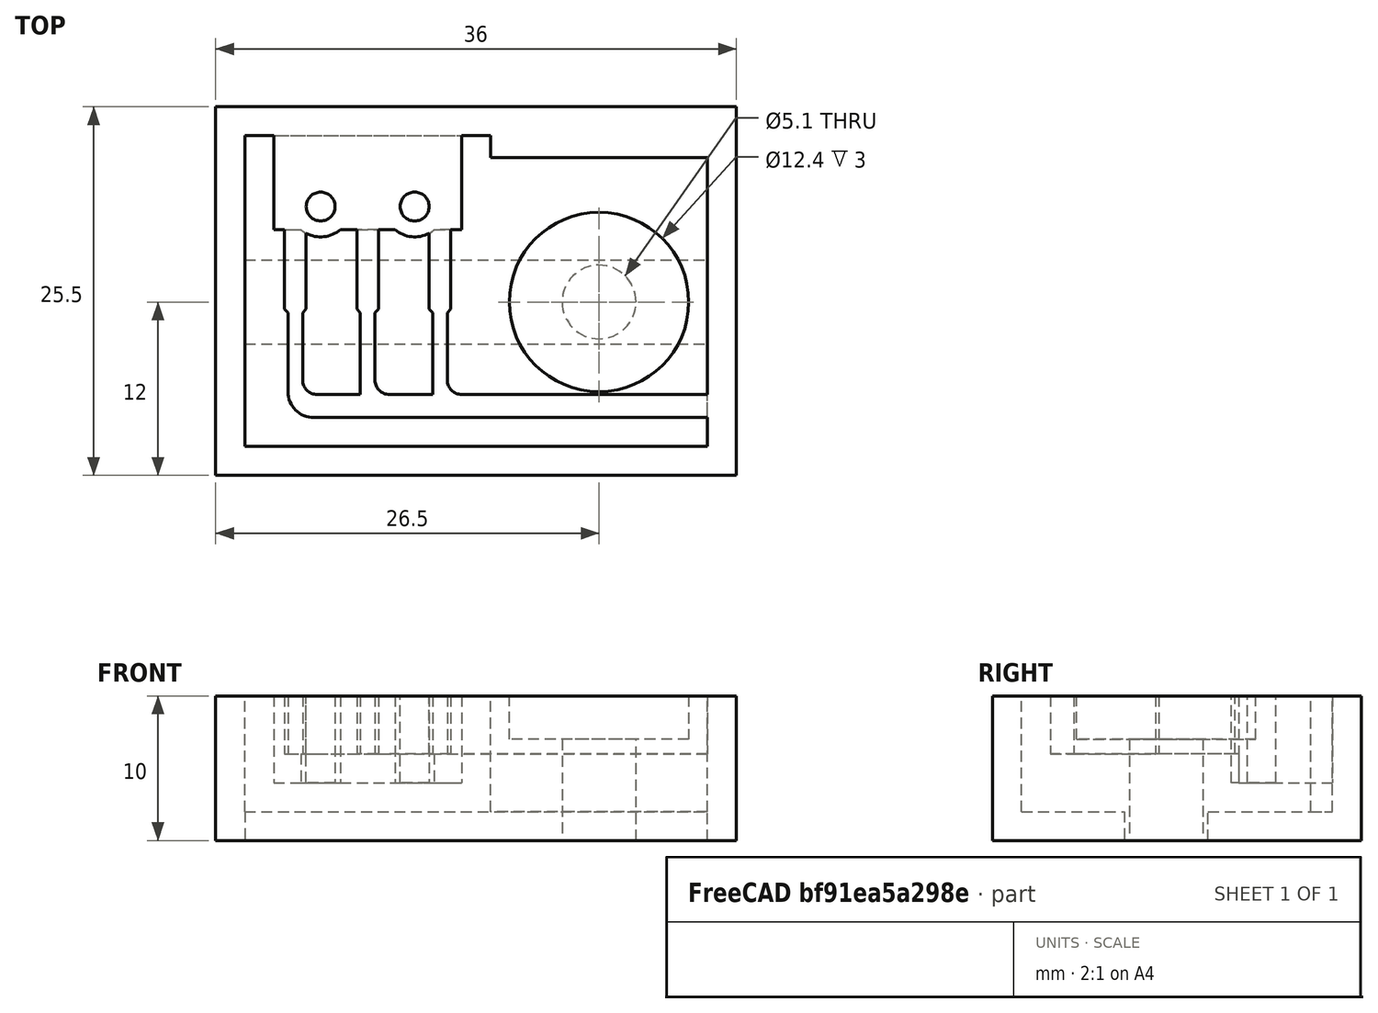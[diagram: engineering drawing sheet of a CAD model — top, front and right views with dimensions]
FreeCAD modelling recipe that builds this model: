
FCSTD DOCUMENT  (FreeCAD 0.18R16131 (Git))
Label: Limit Switch Bed - BottomMirror Job
License: All rights reserved
LicenseURL: http://es.wikipedia.org/wiki/Todos_los_derechos_reservados
objects: Path::FeaturePython×8, Part::Feature×2, Part::FeaturePython×2, Mesh::FeaturePython×1, Part::Mirroring×1, App::FeaturePython×1, App::DocumentObjectGroup×1, Path::FeatureCompoundPython×1
note: 8 computed .brp shape members not serialized (recipe doc carries the construction recipe); baked Part::Feature solids carry a one-line shape summary decoded from their .brp

FEATURE [Part::Feature] Part__Feature  label="_LimitSwitchBed"
  shape: bbox 32 x 21.5 x 10 mm, 57 faces (baked)
FEATURE [Part::Feature] Part__Feature001  label="LimitSwitchBed"
  Placement = pos=(32,0,13) rot=(0,1,0;3.14159rad)
  shape: bbox 32 x 21.5 x 10 mm, 57 faces (baked)
FEATURE [Mesh::FeaturePython] CutMaterial  # WARN: FeaturePython — macro-defined, semantics opaque (R4)
FEATURE [Part::Mirroring] mirror  label="Mirror of LimitSwitchBed"
  Base = (32,0,11)
  Normal = (1,0,0)
  Placement = pos=(-32,0,0) rot=(0,0,1;0rad)
  Source = -> Part__Feature001
FEATURE [App::FeaturePython] SetupSheet  # Path/CAM operation (typed FeaturePython)
  ClearanceHeightExpression = OpStockZMax+SetupSheet.ClearanceHeightOffset
  ClearanceHeightOffset = 5
  FinalDepthExpression = OpFinalDepth
  HorizRapid = 0
  SafeHeightExpression = OpStockZMax+SetupSheet.SafeHeightOffset
  SafeHeightOffset = 3
  StartDepthExpression = OpStartDepth
  StepDownExpression = OpToolDiameter
  VertRapid = 0
FEATURE [Part::FeaturePython] Clone  label="Model-Mirror of LimitSwitchBed"  # Draft clone (typed FeaturePython)
  AttacherType = Attacher::AttachEngine3D
  Fuse = false
  Objects = -> [mirror]
  PathResource = Model
  Placement = pos=(-32,0,0) rot=(0,0,1;0rad)
  Scale = (1,1,1)
FEATURE [App::DocumentObjectGroup] Model
  Group = -> [Clone]
FEATURE [Part::FeaturePython] Stock  # WARN: FeaturePython — macro-defined, semantics opaque (R4)
  Base = -> Model
  ExtXneg = 2
  ExtXpos = 2
  ExtYneg = 2
  ExtYpos = 2
  ExtZneg = 0
  ExtZpos = 0
  StockType = FromBase
FEATURE [Path::FeaturePython] T3__SingleFlute2mm  label="T3: SingleFlute2mm"  # Path/CAM operation (typed FeaturePython)
  HorizFeed = 25
  HorizRapid = 0
  SpindleDir = 0
  SpindleSpeed = 1000
  ToolNumber = 3
  VertFeed = 5
  VertRapid = 0
  expr: HorizRapid = SetupSheet.HorizRapid
  expr: VertRapid = SetupSheet.VertRapid
FEATURE [Path::FeaturePython] T4__SingleFlute1mm  label="T4: SingleFlute1mm"  # Path/CAM operation (typed FeaturePython)
  HorizFeed = 25
  HorizRapid = 0
  SpindleDir = 0
  SpindleSpeed = 1000
  ToolNumber = 4
  VertFeed = 5
  VertRapid = 0
  expr: HorizRapid = SetupSheet.HorizRapid
  expr: VertRapid = SetupSheet.VertRapid
FEATURE [Path::FeaturePython] Pocket_Shape  # Path/CAM operation (typed FeaturePython)
  Active = true
  AreaParams:
    Tolerance = 1e-07
    FitArcs = True
    Simplify = False
    CleanDistance = 0.0
    Accuracy = 0.01
    Unit = 1.0
    MinArcPoints = 4
    MaxArcPoints = 100
    ClipperScale = 10000000.0
    Fill = 0
    Coplanar = 0
    Reorient = True
    Outline = False
    Explode = False
    OpenMode = 0
    Deflection = 0.01
    SubjectFill = 0
    ClipFill = 0
    Offset = 0.0
    ExtraPass = 0
    Stepover = 0.0
    LastStepover = 0.0
    JoinType = 0
    EndType = 0
    MiterLimit = 2.0
    RoundPrecision = 0.0
    PocketMode = 2
    ToolRadius = 1.0
    PocketExtraOffset = 0.0
    PocketStepover = 1.6
    PocketLastStepover = 0.0
    FromCenter = True
    Angle = 45.0
    AngleShift = 0.0
    Shift = 0.0
    Thicken = False
    SectionCount = -1
    Stepdown = 1.0
    SectionOffset = 0.0
    SectionTolerance = 1e-06
    SectionMode = 2
    Project = False
  Base = -> [Clone]
  ClearanceHeight = 15
  CutMode = 0
  ExtraOffset = 0
  FinalDepth = 11
  FinishDepth = 0
  KeepToolDown = false
  MinTravel = false
  OffsetPattern = 1
  OpFinalDepth = 11
  OpStartDepth = 13
  OpStockZMax = 10
  OpStockZMin = 0
  OpToolDiameter = 2
  PathParams = {'orientation': 1, 'feedrate': 25.0, 'feedrate_v': 5.0, 'verbose': True, 'resume_height': 13.0, 'retraction': 15.0, 'return_end': True, 'preamble': False}
  SafeHeight = 13
  StartAt = 0
  StartDepth = 13
  StartPoint = (0,0,0)
  StepDown = 1
  StepOver = 80
  ToolController = -> T3__SingleFlute2mm
  UseOutline = false
  UseStartPoint = false
  ZigZagAngle = 45
  expr: ClearanceHeight = OpStockZMax + SetupSheet.ClearanceHeightOffset
  expr: SafeHeight = OpStockZMax + SetupSheet.SafeHeightOffset
  expr: StepDown = OpToolDiameter / 2
  expr: FinalDepth = OpFinalDepth
  expr: StartDepth = OpStartDepth
FEATURE [Path::FeaturePython] DogboneDressup  # Path/CAM operation (typed FeaturePython)
  Base = -> Pocket_Shape
  BoneBlacklist = [5,6,7,8,9,10,11,12,13,14,15,16,17,18,19,20,21,26]
  Custom = 0
  Incision = 0
  Side = 1
  Style = 1
FEATURE [Path::FeaturePython] Pocket_Shape001  # Path/CAM operation (typed FeaturePython)
  Active = true
  AreaParams:
    Tolerance = 1e-07
    FitArcs = True
    Simplify = False
    CleanDistance = 0.0
    Accuracy = 0.01
    Unit = 1.0
    MinArcPoints = 4
    MaxArcPoints = 100
    ClipperScale = 10000000.0
    Fill = 0
    Coplanar = 0
    Reorient = True
    Outline = False
    Explode = False
    OpenMode = 0
    Deflection = 0.01
    SubjectFill = 0
    ClipFill = 0
    Offset = 0.0
    ExtraPass = 0
    Stepover = 0.0
    LastStepover = 0.0
    JoinType = 0
    EndType = 0
    MiterLimit = 2.0
    RoundPrecision = 0.0
    PocketMode = 2
    ToolRadius = 1.0
    PocketExtraOffset = 0.0
    PocketStepover = 1.6
    PocketLastStepover = 0.0
    FromCenter = True
    Angle = 45.0
    AngleShift = 0.0
    Shift = 0.0
    Thicken = False
    SectionCount = -1
    Stepdown = 1.0
    SectionOffset = 0.0
    SectionTolerance = 1e-06
    SectionMode = 2
    Project = False
  Base = -> [Clone]
  ClearanceHeight = 15
  CutMode = 0
  ExtraOffset = 0
  FinalDepth = 11
  FinishDepth = 0
  KeepToolDown = false
  MinTravel = false
  OffsetPattern = 1
  OpFinalDepth = 11
  OpStartDepth = 13
  OpStockZMax = 10
  OpStockZMin = 0
  OpToolDiameter = 2
  PathParams = {'orientation': 1, 'feedrate': 25.0, 'feedrate_v': 5.0, 'verbose': True, 'resume_height': 13.0, 'retraction': 15.0, 'return_end': True, 'preamble': False}
  SafeHeight = 13
  StartAt = 0
  StartDepth = 13
  StartPoint = (0,0,0)
  StepDown = 1
  StepOver = 80
  ToolController = -> T3__SingleFlute2mm
  UseOutline = false
  UseStartPoint = false
  ZigZagAngle = 45
  expr: ClearanceHeight = OpStockZMax + SetupSheet.ClearanceHeightOffset
  expr: SafeHeight = OpStockZMax + SetupSheet.SafeHeightOffset
  expr: StepDown = OpToolDiameter / 2
  expr: FinalDepth = OpFinalDepth
  expr: StartDepth = OpStartDepth
FEATURE [Path::FeaturePython] DogboneDressup001  # Path/CAM operation (typed FeaturePython)
  Base = -> Pocket_Shape001
  BoneBlacklist = [6,7,8,9,10,11,12,13,14,15,16,17]
  Custom = 0
  Incision = 0
  Side = 1
  Style = 1
FEATURE [Path::FeaturePython] Contour  # Path/CAM operation (typed FeaturePython)
  Active = true
  AreaParams:
    Tolerance = 1e-07
    FitArcs = True
    Simplify = False
    CleanDistance = 0.0
    Accuracy = 0.01
    Unit = 1.0
    MinArcPoints = 4
    MaxArcPoints = 100
    ClipperScale = 10000000.0
    Fill = 0
    Coplanar = 2
    Reorient = True
    Outline = False
    Explode = False
    OpenMode = 0
    Deflection = 0.01
    SubjectFill = 0
    ClipFill = 0
    Offset = 1.0
    ExtraPass = 0
    Stepover = 0.0
    LastStepover = 0.0
    JoinType = 0
    EndType = 0
    MiterLimit = 2.0
    RoundPrecision = 0.0
    PocketMode = 0
    ToolRadius = 1.0
    PocketExtraOffset = 0.0
    PocketStepover = 0.0
    PocketLastStepover = 0.0
    FromCenter = False
    Angle = 45.0
    AngleShift = 0.0
    Shift = 0.0
    Thicken = False
    SectionCount = -1
    Stepdown = 1.0
    SectionOffset = 0.0
    SectionTolerance = 1e-06
    SectionMode = 2
    Project = False
  ClearanceHeight = 17
  Direction = 0
  FinalDepth = 10
  JoinType = 0
  MiterLimit = 0.1
  OffsetExtra = 0
  OpFinalDepth = 0
  OpStartDepth = 10
  OpStockZMax = 10
  OpStockZMin = 0
  OpToolDiameter = 2
  PathParams = {'orientation': 1, 'feedrate': 25.0, 'feedrate_v': 5.0, 'verbose': True, 'resume_height': 15.0, 'retraction': 17.0, 'return_end': True, 'preamble': False}
  SafeHeight = 15
  Side = 0
  StartDepth = 13
  StartPoint = (0,0,0)
  StepDown = 1
  ToolController = -> T3__SingleFlute2mm
  UseComp = true
  UseStartPoint = false
  expr: FinalDepth = 10
  expr: ClearanceHeight = OpStockZMax + SetupSheet.ClearanceHeightOffset + 2mm
  expr: SafeHeight = OpStockZMax + SetupSheet.SafeHeightOffset + 2mm
  expr: StepDown = 1
  expr: StartDepth = OpStartDepth + 3mm
FEATURE [Path::FeatureCompoundPython] Operations  # Path/CAM operation (typed FeaturePython)
  Group = -> [DogboneDressup,DogboneDressup001,Contour]
  UsePlacements = false
FEATURE [Path::FeaturePython] Job  # Path/CAM operation (typed FeaturePython)
  GeometryTolerance = 0.01
  Model = -> Model
  Operations = -> Operations
  PostProcessor = 2
  SetupSheet = -> SetupSheet
  Stock = -> Stock
  ToolController = -> [T3__SingleFlute2mm,T4__SingleFlute1mm]
